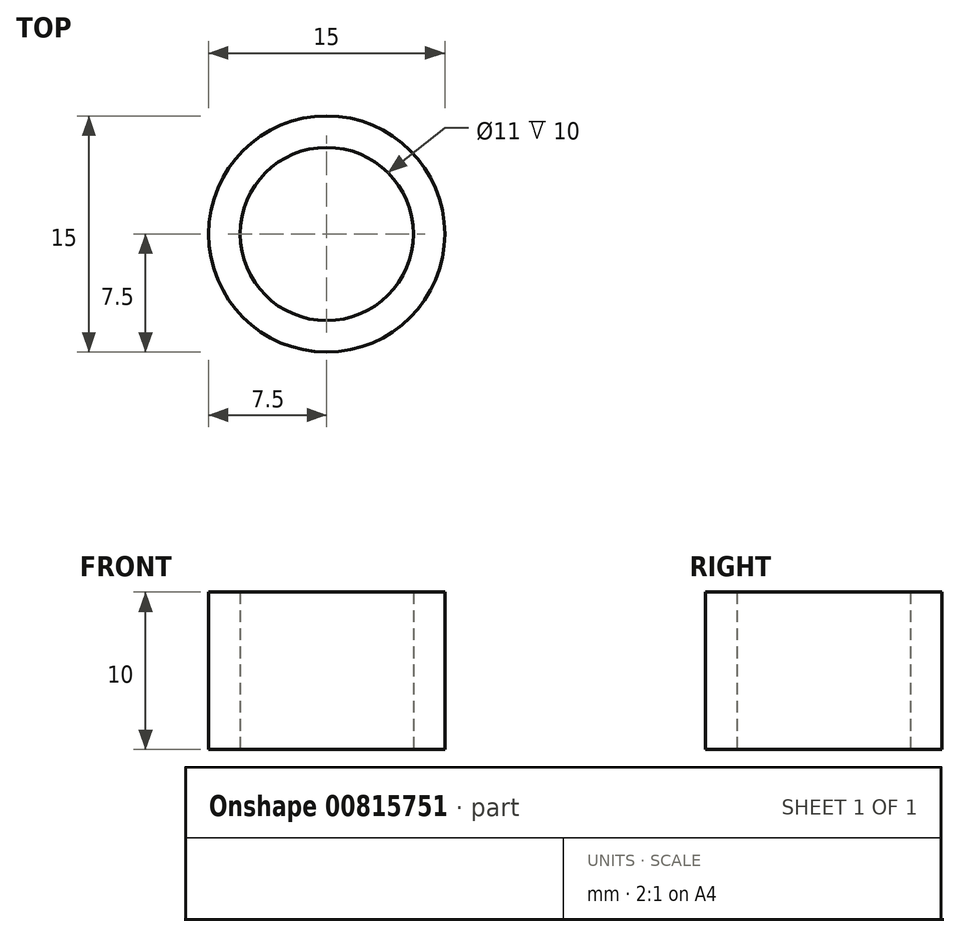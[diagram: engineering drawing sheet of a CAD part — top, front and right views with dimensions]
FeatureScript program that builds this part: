
annotation { "Feature Type Name" : "Feature", "Feature Type Description" : "" }
export const myFeature = defineFeature(function(context is Context, id is Id, definition is map)
    precondition{}
    {
        {
            var Q0;
            Q0=qCreatedBy(makeId("Top.planeOp"),FACE);
            var sketch = newSketch(context, id + "F0", { "sketchPlane" : qUnion([Q0])});
            skCircle(sketch, "E0", {"center": v(0, 0) * mm, "radius": 7.5 * mm});
            skCircle(sketch, "E1", {"center": v(0, 0) * mm, "radius": 5.5 * mm});
            skSolve(sketch);
        }
        {
            var Q0;
            Q0=makeQuery(id+"F0.imprint","IMPRINT",FACE,{"disambiguationData":[TD([[makeQuery(id+"F0.imprint","IMPRINT",EDGE,{"derivedFrom":sQuery(id+"F0.wireOp",EDGE,"E0")}),1.0]])]});
            extrude(context, id + "F1", {"entities" : qUnion([Q0]), "depth" : 10 * mm, "offsetDistance" : 25.4 * mm});
        }
    });
